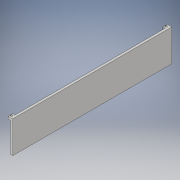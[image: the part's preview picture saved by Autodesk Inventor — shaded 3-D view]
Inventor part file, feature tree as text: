
AUTODESK INVENTOR PART (.ipt)
format: ipt  version: 2017 (Build 210142000, 142)  size: 150,528 bytes
history: native  units: in
note: dims shown in document units (in); Inventor stores cm internally (conversion verified against a paired STEP export)
features: sketch x4, extrude x2, hole x2
ambient origin geometry x8: Origin, YZ Plane, XZ Plane, XY Plane, X Axis, Y Axis, Z Axis, Center Point
bodies: Solid1 (feature_tree)
feature tree (8):
  extrude  "Extrusion1"  Depth=17.5in
  extrude  "Extrusion2"  Depth=0.5in
  sketch  "Sketch3"  dims[d5=0.25in d6=0.25in]
  sketch  "Sketch4"  dims[d7=0.5in d8=0.25in d9=0.5in d10=0.5in d11=3.5in d12=3.5in d13=0.25in d14=0.0in d15=0.25in d16=0.25in d17=0.25in d33=0.125in d34=0.25in d35=0.125in d36=0.25in d37=0.2in d38=0.75in d39=0.375in d40=0.25in d41=0.5635in d42=0.25in d43=0.8108in d44=0.125in d45=0.25in d46=0.25in d47=0.125in d48=0.2in d49=0.75in d50=0.375in d51=0.25in d52=0.5635in d53=0.25in d54=0.8108in]
  hole  "Hole3"  [1 undecoded]
  hole  "Hole4"  [1 undecoded]
  sketch  "Sketch1"  dims[d0=3.5in d1=17.5in]
  sketch  "Sketch2"  dims[d2=0.25in d3=0.0in d4=0.5in]
note: 2 required parameter values undecoded (feature->parameter linkage not recoverable at this tier; creation-order binding heuristic only, values carry confidence <= 0.55)
